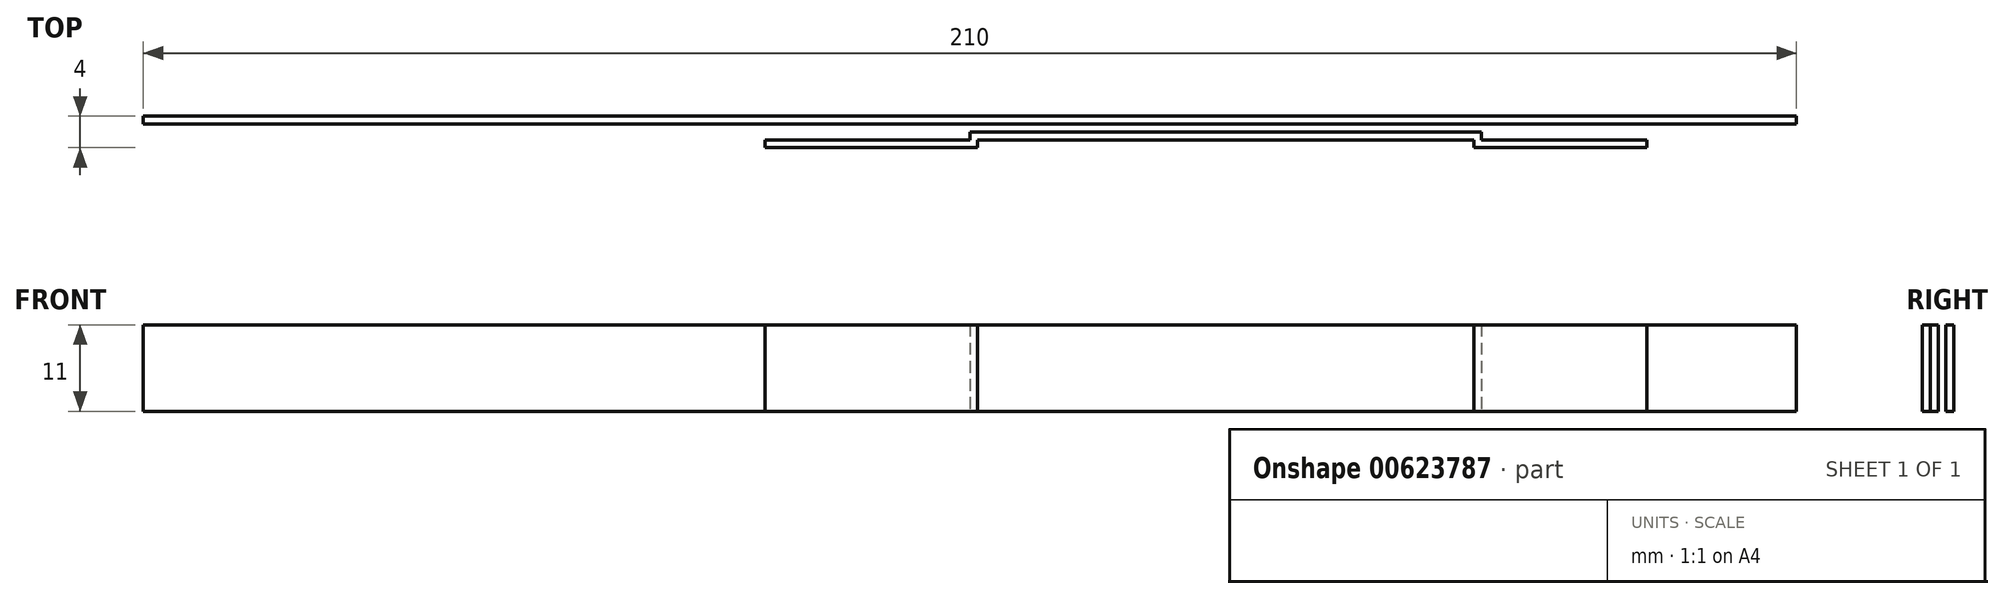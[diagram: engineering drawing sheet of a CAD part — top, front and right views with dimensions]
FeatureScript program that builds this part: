
annotation { "Feature Type Name" : "Feature", "Feature Type Description" : "" }
export const myFeature = defineFeature(function(context is Context, id is Id, definition is map)
    precondition{}
    {
        {
            var Q0;
            Q0=qCreatedBy(makeId("Top.planeOp"),FACE);
            var sketch = newSketch(context, id + "F0", { "sketchPlane" : qUnion([Q0])});
            skLineSegment(sketch, "E0.bottom", {"start": v(-105, -10) * mm, "end": v(105, -10) * mm});
            skLineSegment(sketch, "E0.top", {"start": v(-105, -13) * mm, "end": v(105, -13) * mm});
            skLineSegment(sketch, "E0.left", {"start": v(-105, -10) * mm, "end": v(-105, -13) * mm});
            skLineSegment(sketch, "E0.right", {"start": v(105, -10) * mm, "end": v(105, -13) * mm});
            skLineSegment(sketch, "E1", {"start": v(0, 0) * mm, "end": v(0, -10) * mm, "construction": true});
            skLineSegment(sketch, "E2", {"start": v(-105, -10) * mm, "end": v(0, -10) * mm, "construction": true});
            skLineSegment(sketch, "E3.top", {"start": v(-105, -11) * mm, "end": v(105, -11) * mm});
            skLineSegment(sketch, "E3.left", {"start": v(-105, -10) * mm, "end": v(-105, -11) * mm});
            skLineSegment(sketch, "E3.right", {"start": v(105, -10) * mm, "end": v(105, -11) * mm});
            skLineSegment(sketch, "E4.top", {"start": v(-105, -12) * mm, "end": v(105, -12) * mm});
            skLineSegment(sketch, "E4.left", {"start": v(-105, -13) * mm, "end": v(-105, -12) * mm});
            skLineSegment(sketch, "E4.right", {"start": v(105, -13) * mm, "end": v(105, -12) * mm});
            skLineSegment(sketch, "E5", {"start": v(-105, -13) * mm, "end": v(-26, -13) * mm, "construction": true});
            skLineSegment(sketch, "E6.bottom", {"start": v(-26, -13) * mm, "end": v(1, -13) * mm});
            skLineSegment(sketch, "E6.top", {"start": v(-26, -14) * mm, "end": v(1, -14) * mm});
            skLineSegment(sketch, "E6.left", {"start": v(-26, -13) * mm, "end": v(-26, -14) * mm});
            skLineSegment(sketch, "E6.right", {"start": v(1, -13) * mm, "end": v(1, -14) * mm});
            skLineSegment(sketch, "E7.bottom", {"start": v(-25, -13) * mm, "end": v(0, -13) * mm});
            skLineSegment(sketch, "E7.top", {"start": v(-25, -12) * mm, "end": v(0, -12) * mm});
            skLineSegment(sketch, "E7.left", {"start": v(-25, -13) * mm, "end": v(-25, -12) * mm});
            skLineSegment(sketch, "E7.right", {"start": v(0, -13) * mm, "end": v(0, -12) * mm});
            skLineSegment(sketch, "E8", {"start": v(-26, -13) * mm, "end": v(-25, -13) * mm, "construction": true});
            skLineSegment(sketch, "E9.bottom", {"start": v(65, -12) * mm, "end": v(85, -12) * mm});
            skLineSegment(sketch, "E9.top", {"start": v(65, -13) * mm, "end": v(85, -13) * mm});
            skLineSegment(sketch, "E9.left", {"start": v(65, -12) * mm, "end": v(65, -13) * mm});
            skLineSegment(sketch, "E9.right", {"start": v(85, -12) * mm, "end": v(85, -13) * mm});
            skLineSegment(sketch, "E10", {"start": v(0, -12) * mm, "end": v(65, -12) * mm, "construction": true});
            skLineSegment(sketch, "E11.bottom", {"start": v(64, -13) * mm, "end": v(86, -13) * mm});
            skLineSegment(sketch, "E11.top", {"start": v(64, -14) * mm, "end": v(86, -14) * mm});
            skLineSegment(sketch, "E11.left", {"start": v(64, -13) * mm, "end": v(64, -14) * mm});
            skLineSegment(sketch, "E11.right", {"start": v(86, -13) * mm, "end": v(86, -14) * mm});
            skLineSegment(sketch, "E12", {"start": v(64, -13) * mm, "end": v(65, -13) * mm, "construction": true});
            skSolve(sketch);
        }
        {
            var Q0;
            {var subQ1=sQuery(id+"F0.wireOp",EDGE,"E0.left");Q0=makeQuery(id+"F0.imprint","IMPRINT",FACE,{"disambiguationData":[TD([[makeQuery(id+"F0.imprint","IMPRINT",EDGE,{"derivedFrom":subQ1}),1.0]])]});}
            var Q1;
            Q1=makeQuery(id+"F0.imprint","IMPRINT",FACE,{"disambiguationData":[TD([[makeQuery(id+"F0.imprint","IMPRINT",EDGE,{"derivedFrom":sQuery(id+"F0.wireOp",EDGE,"E9.bottom")}),-1.0]])]});
            var Q2;
            Q2=makeQuery(id+"F0.imprint","IMPRINT",FACE,{"disambiguationData":[TD([[makeQuery(id+"F0.imprint","IMPRINT",EDGE,{"derivedFrom":sQuery(id+"F0.wireOp",EDGE,"E7.bottom")}),1.0]])]});
            extrude(context, id + "F1", {"entities" : qUnion([Q0, Q1, Q2]), "depth" : 1 * mm, "offsetDistance" : 25 * mm});
        }
        {
            var Q0;
            Q0=makeQuery(id+"F0.imprint","IMPRINT",FACE,{"disambiguationData":[TD([[makeQuery(id+"F0.imprint","IMPRINT",EDGE,{"derivedFrom":sQuery(id+"F0.wireOp",EDGE,"E0.bottom")}),-1.0]])]});
            var Q1;
            Q1=makeQuery(id+"F0.imprint","IMPRINT",FACE,{"disambiguationData":[TD([[makeQuery(id+"F0.imprint","IMPRINT",EDGE,{"derivedFrom":sQuery(id+"F0.wireOp",EDGE,"E6.top")}),1.0]])]});
            var Q2;
            {var subQ0=sQuery(id+"F0.wireOp",EDGE,"E4.left");Q2=makeQuery(id+"F0.imprint","IMPRINT",FACE,{"disambiguationData":[TD([[makeQuery(id+"F0.imprint","IMPRINT",EDGE,{"derivedFrom":subQ0}),-1.0]])]});}
            var Q3;
            {var subQ3=sQuery(id+"F0.wireOp",EDGE,"E7.right");Q3=makeQuery(id+"F0.imprint","IMPRINT",FACE,{"disambiguationData":[TD([[makeQuery(id+"F0.imprint","IMPRINT",EDGE,{"derivedFrom":subQ3}),-1.0]])]});}
            var Q4;
            Q4=makeQuery(id+"F0.imprint","IMPRINT",FACE,{"disambiguationData":[TD([[makeQuery(id+"F0.imprint","IMPRINT",EDGE,{"derivedFrom":sQuery(id+"F0.wireOp",EDGE,"E11.top")}),1.0]])]});
            var Q5;
            {var subQ1=sQuery(id+"F0.wireOp",EDGE,"E4.right");Q5=makeQuery(id+"F0.imprint","IMPRINT",FACE,{"disambiguationData":[TD([[makeQuery(id+"F0.imprint","IMPRINT",EDGE,{"derivedFrom":subQ1}),1.0]])]});}
            extrude(context, id + "F2", {"entities" : qUnion([Q0, Q1, Q2, Q3, Q4, Q5]), "operationType" : NewBodyOperationType.ADD, "depth" : 11 * mm, "offsetDistance" : 25 * mm});
        }
    });
